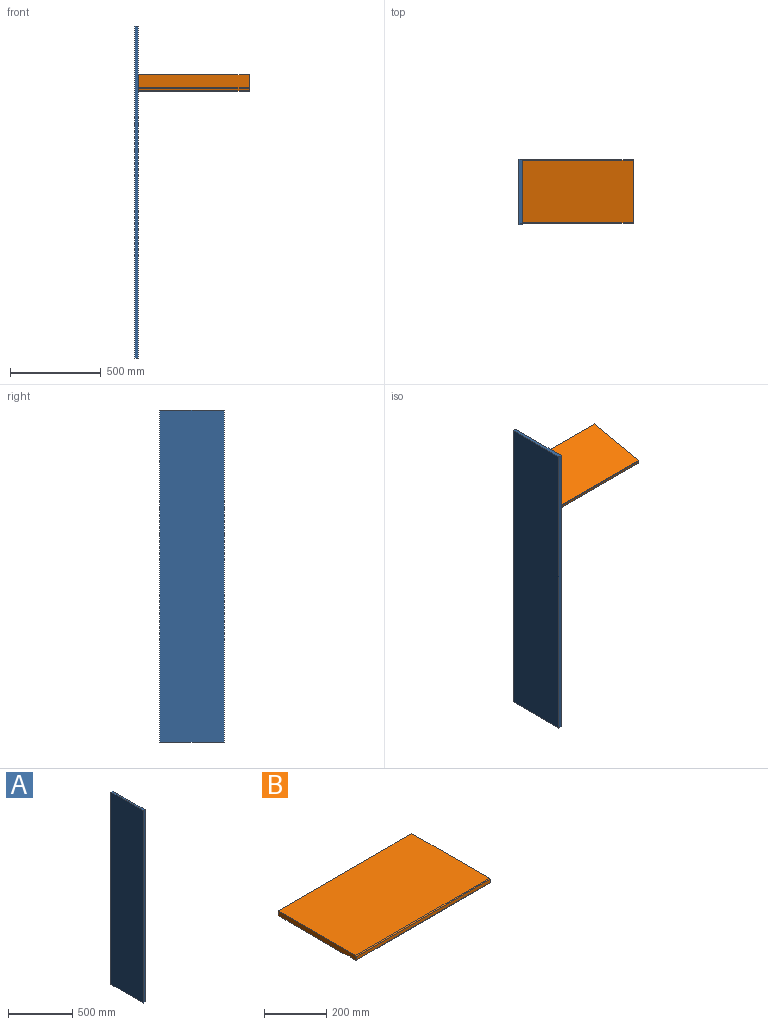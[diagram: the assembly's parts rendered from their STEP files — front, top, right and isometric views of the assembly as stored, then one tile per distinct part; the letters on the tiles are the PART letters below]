
ASSEMBLY  parts=2 mates=1
PART A: 14 faces, bbox 19.1x355.6x1828.8 mm
  f0: plane 355.6x19.05mm, normal (0,0,-1), area 6774.2mm2, adj f1,f3,f4,f5
  f1: plane 1828.8x19.05mm, normal (0,1,0), area 34838.6mm2, adj f0,f2,f4,f5
  f2: plane 355.6x19.05mm, normal (0,0,1), area 6774.2mm2, adj f1,f3,f4,f5
  f3: plane 1828.8x19.05mm, normal (0,-1,0), area 34838.6mm2, adj f0,f2,f4,f5
  f4: plane 1828.8x355.6mm, normal (1,0,0), area 650230.7mm2, adj f0,f1,f2,f3,f7,f9,f11,f13
  f5: plane 1828.8x355.6mm, normal (-1,0,0), area 650321.3mm2, adj f0,f1,f2,f3
  f6: cone r=0mm half-angle=59deg, axis (1,0,0), area 22.9mm2, adj f7
  f7: cylinder r=2.5mm len=9.53mm, axis (1,0,0), area 149.6mm2, adj f4,f6
  f8: cone r=0mm half-angle=59deg, axis (1,0,0), area 22.9mm2, adj f9
  f9: cylinder r=2.5mm len=9.53mm, axis (1,0,0), area 149.6mm2, adj f4,f8
  f10: cone r=0mm half-angle=59deg, axis (1,0,0), area 22.9mm2, adj f11
  f11: cylinder r=2.5mm len=9.53mm, axis (1,0,0), area 149.6mm2, adj f4,f10
  f12: cone r=0mm half-angle=59deg, axis (1,0,0), area 36.9mm2, adj f13
  f13: cylinder r=3.17mm len=9.53mm, axis (1,0,0), area 190mm2, adj f4,f12
PART B: 16 faces, bbox 609.6x355.6x19.1 mm
  f0: plane 355.6x19.05mm, normal (-1,0,0), area 6704.3mm2, adj f1,f2,f4,f5,f6,f8,f9,f11
  f1: plane 609.6x352.43mm, normal (0,0,-1), area 214576.2mm2, adj f0,f3,f4,f6,f7,f8,f10,f11
  f2: plane 609.6x12.7mm, normal (0,-1,0), area 7741.9mm2, adj f0,f3,f14,f15
  f3: plane 355.6x19.05mm, normal (1,0,0), area 6769.9mm2, adj f1,f2,f4,f5,f14,f15
  f4: plane 609.6x19.05mm, normal (0,1,0), area 11612.9mm2, adj f0,f1,f3,f5
  f5: plane 609.6x352.43mm, normal (0,0,1), area 214838.3mm2, adj f0,f3,f4,f15
  f6: plane 12.7x3.18mm, normal (0,-1,0), area 40.3mm2, adj f0,f1,f7,f9
  f7: plane 6.35x3.18mm, normal (-1,0,0), area 20.2mm2, adj f1,f6,f8,f9
  f8: plane 12.7x3.18mm, normal (0,1,0), area 40.3mm2, adj f0,f1,f7,f9
  f9: plane 12.7x6.35mm, normal (0,0,-1), area 80.6mm2, adj f0,f6,f7,f8
  f10: plane 14.29x3.18mm, normal (-1,0,0), area 45.4mm2, adj f1,f11,f12,f13
  f11: plane 12.7x3.18mm, normal (0,1,0), area 40.3mm2, adj f0,f1,f10,f13
  f12: plane 12.7x3.18mm, normal (0,-1,0), area 40.3mm2, adj f0,f1,f10,f13
  f13: plane 14.29x12.7mm, normal (0,0,-1), area 181.5mm2, adj f0,f10,f11,f12
  f14: cylinder r=3.17mm len=609.6mm, axis (1,0,0), area 3040.2mm2, adj f0,f1,f2,f3
  f15: cylinder r=3.17mm len=609.6mm, axis (-1,0,0), area 3040.2mm2, adj f0,f2,f3,f5
PLACE A t=(-417.08,-427.8,-62.63)mm fixed
PLACE B rot(axis=(1,0,0),12.1deg) t=(-93.23,-424.05,528.59)mm
MATE revolute B.f0 <-> A.f8  axis (-1,0,0) through (-398.03,-288.1,560.93)mm
